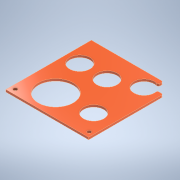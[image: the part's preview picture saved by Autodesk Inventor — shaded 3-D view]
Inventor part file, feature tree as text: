
AUTODESK INVENTOR PART (.ipt)
format: ipt  version: 2021 (Build 250183000, 183)  size: 180,224 bytes
history: native  units: mm
features: sketch x3, extrude x2, hole x1
ambient origin geometry x8: Origin, YZ Plane, XZ Plane, XY Plane, X Axis, Y Axis, Z Axis, Center Point
bodies: Solid1 (feature_tree)
feature tree (6):
  extrude  "Extrusion1"  Depth=3.0mm TaperAngle=0.0deg
  hole  "Hole1"  [1 undecoded]
  extrude  "Extrusion2"  Depth=2.0mm
  sketch  "Sketch1"  dims[d0=47.7mm d1=27.7mm d2=27.7mm d3=27.7mm d4=27.7mm d5=116.5mm d6=112.5mm d7=37.0mm d8=18.5mm d9=30.9mm d10=19.5mm d11=35.0mm d12=35.0mm d13=25.8mm d14=28.0mm d15=3.0mm d16=0.0mm]
  sketch  "Sketch2"  dims[d20=112.5mm d21=56.25mm]
  sketch  "Sketch3"  dims[d22=58.25mm d23=116.5mm d24=23.25mm d25=35.0mm d26=35.0mm d27=19.25mm d28=37.75mm d29=30.25mm d30=2.0mm d31=2.0mm d32=15.0mm d33=15.0mm d34=2.0mm d35=7.0mm d36=6.0mm d37=6.0mm d38=5.0mm d39=6.0mm d40=4.0mm d41=2.0mm d42=90.0deg d43=8.0mm d44=20.594885mm d45=0.3mm d46=0.0mm]
note: 1 required parameter value undecoded (feature->parameter linkage not recoverable at this tier; creation-order binding heuristic only, values carry confidence <= 0.55)
